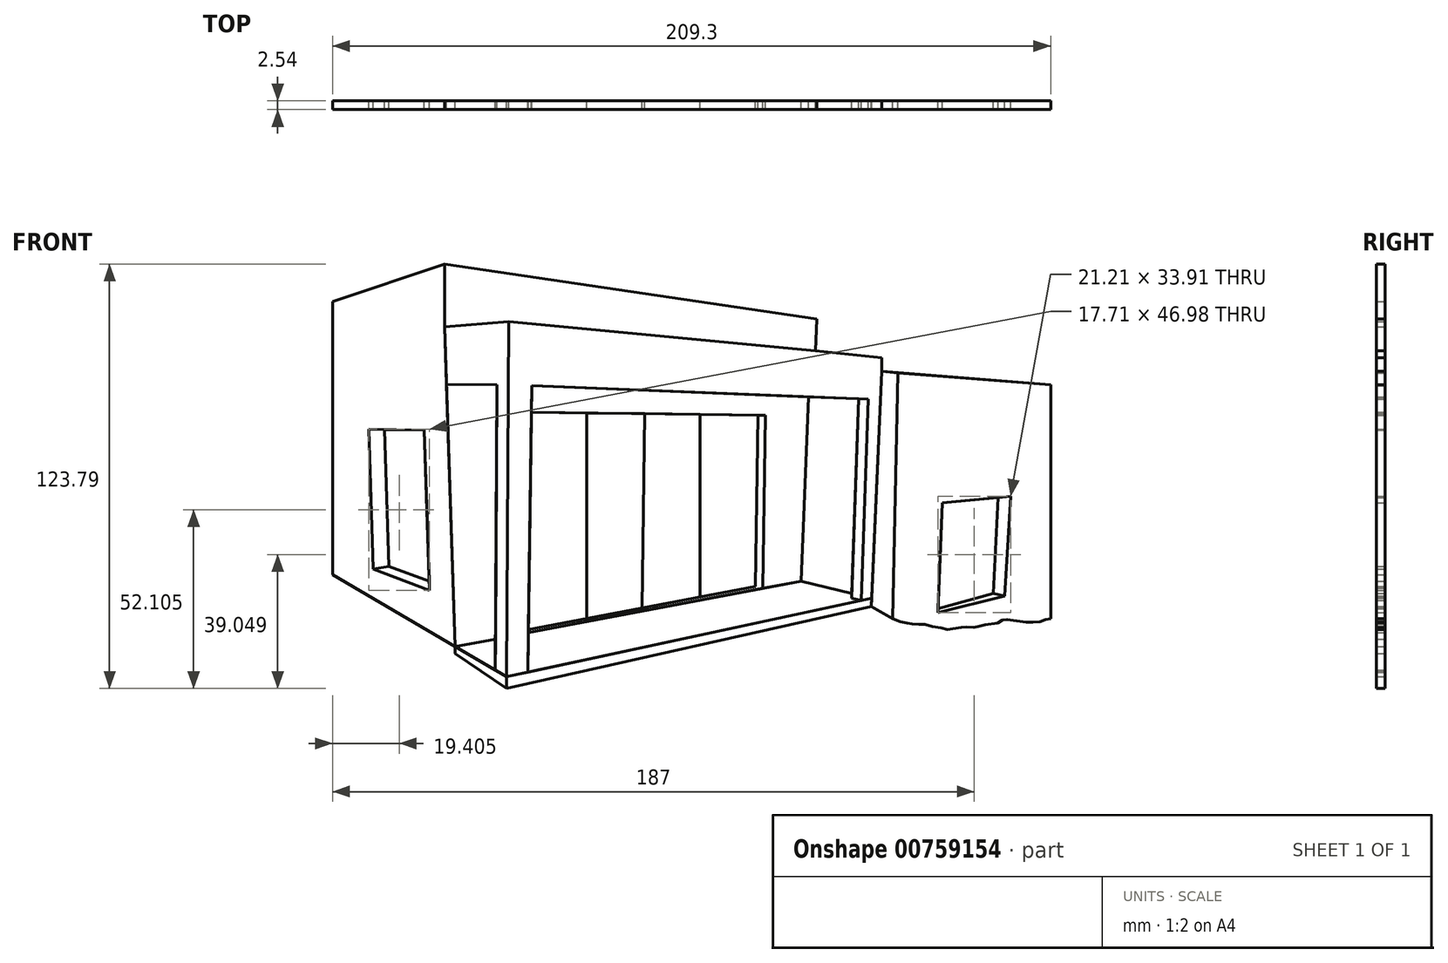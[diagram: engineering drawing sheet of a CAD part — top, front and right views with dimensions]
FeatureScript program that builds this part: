
annotation { "Feature Type Name" : "Feature", "Feature Type Description" : "" }
export const myFeature = defineFeature(function(context is Context, id is Id, definition is map)
    precondition{}
    {
        {
            var Q0;
            Q0=qCreatedBy(makeId("Front.planeOp"),FACE);
            var sketch = newSketch(context, id + "F0", { "sketchPlane" : qUnion([Q0])});
            skSolve(sketch);
        }
        {
            var Q0;
            Q0=qCreatedBy(makeId("Front.planeOp"),FACE);
            var sketch = newSketch(context, id + "F1", { "sketchPlane" : qUnion([Q0])});
            skPoint(sketch, "E0.0", {"position": v(-106.72, 78.02) * mm});
            skPoint(sketch, "E1.0", {"position": v(102.58, 78.02) * mm});
            skPoint(sketch, "E2.0", {"position": v(102.58, -78.96) * mm});
            skPoint(sketch, "E3.0", {"position": v(-106.72, -78.96) * mm});
            skLineSegment(sketch, "E4", {"start": v(-106.72, 78.02) * mm, "end": v(102.58, 78.02) * mm});
            skLineSegment(sketch, "E5", {"start": v(102.58, 78.02) * mm, "end": v(102.58, -78.96) * mm});
            skLineSegment(sketch, "E6", {"start": v(102.58, -78.96) * mm, "end": v(-106.72, -78.96) * mm});
            skLineSegment(sketch, "E7", {"start": v(-106.72, -78.96) * mm, "end": v(-106.72, 78.02) * mm});
            skLineSegment(sketch, "E8", {"start": v(-106.72, 62.84) * mm, "end": v(-74.06, 73.78) * mm});
            skLineSegment(sketch, "E9", {"start": v(-74.06, 73.78) * mm, "end": v(34.35, 57.7) * mm});
            skLineSegment(sketch, "E10", {"start": v(34.35, 57.7) * mm, "end": v(34.04, 48.47) * mm});
            skLineSegment(sketch, "E11", {"start": v(34.04, 48.47) * mm, "end": v(53.34, 46.39) * mm});
            skLineSegment(sketch, "E12", {"start": v(53.34, 46.39) * mm, "end": v(53.34, 42.5) * mm});
            skLineSegment(sketch, "E13", {"start": v(53.34, 42.5) * mm, "end": v(57.96, 41.92) * mm});
            skLineSegment(sketch, "E14", {"start": v(57.96, 41.92) * mm, "end": v(102.58, 38.55) * mm});
            skLineSegment(sketch, "E15", {"start": v(57.96, 41.92) * mm, "end": v(56.56, -29.63) * mm});
            skLineSegment(sketch, "E16", {"start": v(70.93, 4.17) * mm, "end": v(69.68, -27.92) * mm});
            skLineSegment(sketch, "E17", {"start": v(69.68, -27.92) * mm, "end": v(89.2, -23) * mm});
            skLineSegment(sketch, "E18", {"start": v(89.2, -23) * mm, "end": v(90.88, 6) * mm});
            skLineSegment(sketch, "E19", {"start": v(90.88, 6) * mm, "end": v(70.93, 4.17) * mm});
            skLineSegment(sketch, "E20", {"start": v(85.86, -22.34) * mm, "end": v(89.2, -23) * mm});
            skLineSegment(sketch, "E21", {"start": v(-74.06, 73.78) * mm, "end": v(-74.06, 55.43) * mm});
            skLineSegment(sketch, "E22", {"start": v(-74.06, 55.43) * mm, "end": v(-55.39, 57.02) * mm});
            skLineSegment(sketch, "E23", {"start": v(-55.39, 57.02) * mm, "end": v(34.04, 48.47) * mm});
            skLineSegment(sketch, "E24", {"start": v(-49.82, -45) * mm, "end": v(-48.69, 38.29) * mm});
            skLineSegment(sketch, "E25", {"start": v(-48.69, 38.29) * mm, "end": v(49.42, 34.34) * mm});
            skLineSegment(sketch, "E26", {"start": v(53.34, 42.5) * mm, "end": v(50.25, -26.04) * mm});
            skLineSegment(sketch, "E27", {"start": v(50.25, -26.04) * mm, "end": v(56.56, -29.63) * mm});
            skLineSegment(sketch, "E28", {"start": v(53.34, 42.5) * mm, "end": v(102.58, 38.55) * mm});
            skLineSegment(sketch, "E29", {"start": v(47.33, -24.3) * mm, "end": v(49.42, 34.34) * mm});
            skLineSegment(sketch, "E30", {"start": v(-106.72, -16.86) * mm, "end": v(-70.99, -37.79) * mm});
            skLineSegment(sketch, "E31", {"start": v(-70.99, -37.79) * mm, "end": v(-74.06, 55.43) * mm});
            skLineSegment(sketch, "E32", {"start": v(50.25, -26.04) * mm, "end": v(-51.74, -49.05) * mm});
            skLineSegment(sketch, "E33", {"start": v(50.36, -23.64) * mm, "end": v(-56, -46.56) * mm});
            skLineSegment(sketch, "E34", {"start": v(-70.99, -37.79) * mm, "end": v(-56, -46.56) * mm});
            skLineSegment(sketch, "E35", {"start": v(-56, -46.56) * mm, "end": v(-55.5, 38.54) * mm});
            skLineSegment(sketch, "E36", {"start": v(-58.8, 38.56) * mm, "end": v(-73.5, 38.64) * mm});
            skLineSegment(sketch, "E37", {"start": v(-55.5, 38.54) * mm, "end": v(-55.39, 57.02) * mm});
            skLineSegment(sketch, "E38", {"start": v(-80, 25.4) * mm, "end": v(-78.46, -21.4) * mm});
            skLineSegment(sketch, "E39", {"start": v(-78.46, -21.4) * mm, "end": v(-94.83, -15.13) * mm});
            skLineSegment(sketch, "E40", {"start": v(-94.83, -15.13) * mm, "end": v(-96.17, 25.59) * mm});
            skLineSegment(sketch, "E41", {"start": v(-96.17, 25.59) * mm, "end": v(-80, 25.4) * mm});
            skLineSegment(sketch, "E42", {"start": v(-94.83, -15.13) * mm, "end": v(-90.28, -14.41) * mm});
            skLineSegment(sketch, "E43", {"start": v(29.88, -18.67) * mm, "end": v(32.04, 35.04) * mm});
            skLineSegment(sketch, "E44", {"start": v(29.88, -18.67) * mm, "end": v(44.61, -22.24) * mm});
            skLineSegment(sketch, "E45", {"start": v(29.88, -18.67) * mm, "end": v(-49.67, -33.74) * mm});
            skLineSegment(sketch, "E46", {"start": v(-59.3, -44.63) * mm, "end": v(-58.8, 38.56) * mm});
            skLineSegment(sketch, "E47", {"start": v(47.33, -24.3) * mm, "end": v(44.56, -23.62) * mm});
            skLineSegment(sketch, "E48", {"start": v(44.56, -23.62) * mm, "end": v(46.64, 34.45) * mm});
            skLineSegment(sketch, "E49", {"start": v(-56, -46.56) * mm, "end": v(-56, -50.01) * mm});
            skLineSegment(sketch, "E50", {"start": v(-51.74, -49.05) * mm, "end": v(-56, -50.01) * mm});
            skLineSegment(sketch, "E51", {"start": v(-56, -50.01) * mm, "end": v(-70.99, -39.84) * mm});
            skLineSegment(sketch, "E52", {"start": v(-70.99, -39.84) * mm, "end": v(-70.99, -37.79) * mm});
            skLineSegment(sketch, "E53.trimOffspring", {"start": v(-59.24, -35.56) * mm, "end": v(-70.99, -37.79) * mm});
            skLineSegment(sketch, "E54", {"start": v(-48.8, 30.57) * mm, "end": v(19.35, 29.64) * mm});
            skLineSegment(sketch, "E55", {"start": v(19.35, 29.64) * mm, "end": v(18.66, -20.8) * mm});
            skLineSegment(sketch, "E56", {"start": v(18.66, -20.8) * mm, "end": v(16.55, -20.28) * mm});
            skLineSegment(sketch, "E57", {"start": v(16.55, -20.28) * mm, "end": v(17.23, 29.67) * mm});
            skLineSegment(sketch, "E58", {"start": v(16.55, -20.28) * mm, "end": v(-49.66, -32.83) * mm});
            skPoint(sketch, "E59", {"position": v(-16.55, -26.55) * mm});
            skLineSegment(sketch, "E60", {"start": v(-16.55, -26.55) * mm, "end": v(-15.78, 30.1) * mm});
            skPoint(sketch, "E60.endSnap0", {"position": v(-14.72, 30.1) * mm});
            skLineSegment(sketch, "E61", {"start": v(0.32, 29.9) * mm, "end": v(0.32, -23.35) * mm});
            skLineSegment(sketch, "E62", {"start": v(-32.7, 0.1) * mm, "end": v(-32.7, 30.35) * mm});
            skLineSegment(sketch, "E63", {"start": v(-32.7, 30.35) * mm, "end": v(-32.7, -29.61) * mm});
            skFitSpline(sketch, "E64", {"points": [v(56.56, -29.63) * mm, v(58.65, -30.57) * mm, v(60.12, -30.68) * mm, v(61.48, -31.2) * mm, v(62.1, -31.2) * mm, v(63.62, -31.25) * mm, v(64.87, -31.3) * mm, v(66.07, -31.36) * mm, v(68, -31.88) * mm, v(70.57, -32.35) * mm, v(72.12, -32.87) * mm, v(73.49, -32.54) * mm, v(74.26, -32.5) * mm, v(76.7, -32.13) * mm, v(77.4, -32.06) * mm, v(78.47, -32.06) * mm, v(80.36, -32.13) * mm, v(80.91, -32.06) * mm, v(81.46, -31.87) * mm, v(82.46, -31.54) * mm, v(87.38, -30.83) * mm, v(88.19, -30.31) * mm, v(88.92, -29.95) * mm, v(89.31, -29.9) * mm, v(90.88, -29.95) * mm, v(94.9, -30.72) * mm, v(96, -30.62) * mm, v(97.98, -30.62) * mm, v(99.55, -30.57) * mm, v(100.8, -30.2) * mm, v(101.58, -29.63) * mm, v(102.58, -29.63) * mm], "startDerivative": vector(52.93, -29.96) * mm, "endDerivative": vector(39.36, -6.16) * mm});
            skLineSegment(sketch, "E65", {"start": v(-49.82, -45) * mm, "end": v(-49.82, -45.23) * mm});
            skLineSegment(sketch, "E66", {"start": v(-15.78, 30.1) * mm, "end": v(-15.78, 30.12) * mm});
            skLineSegment(sketch, "E67", {"start": v(-78.55, -18.72) * mm, "end": v(-90.28, -14.41) * mm});
            skLineSegment(sketch, "E68", {"start": v(-90.28, -14.41) * mm, "end": v(-91.6, 25.53) * mm});
            skPoint(sketch, "E69.start.orphan", {"position": v(-88.09, 25.5) * mm});
            skLineSegment(sketch, "E70", {"start": v(69.72, -26.75) * mm, "end": v(85.86, -22.34) * mm});
            skLineSegment(sketch, "E71", {"start": v(85.86, -22.34) * mm, "end": v(87.24, 5.45) * mm});
            skLineSegment(sketch, "E72", {"start": v(87.24, 5.45) * mm, "end": v(87.25, 5.66) * mm});
            skPoint(sketch, "E73.start.orphan", {"position": v(84.93, 5.45) * mm});
            skSolve(sketch);
        }
        {
            var Q0;
            {var subQ1=sQuery(id+"F1.wireOp",EDGE,"E8");Q0=makeQuery(id+"F1.imprint","IMPRINT",FACE,{"disambiguationData":[TD([[makeQuery(id+"F1.imprint","IMPRINT",EDGE,{"derivedFrom":subQ1}),-1.0]])]});}
            extrude(context, id + "F2", {"entities" : qUnion([Q0]), "depth" : 2.54 * mm, "offsetDistance" : 25.4 * mm});
        }
        {
            var Q0;
            Q0=makeQuery(id+"F1.imprint","IMPRINT",FACE,{"disambiguationData":[TD([[makeQuery(id+"F1.imprint","IMPRINT",EDGE,{"derivedFrom":sQuery(id+"F1.wireOp",EDGE,"E9")}),-1.0]])]});
            extrude(context, id + "F3", {"entities" : qUnion([Q0]), "depth" : 2.54 * mm, "offsetDistance" : 25.4 * mm});
        }
        {
            var Q0;
            {var subQ4=sQuery(id+"F1.wireOp",EDGE,"E14");Q0=makeQuery(id+"F1.imprint","IMPRINT",FACE,{"disambiguationData":[TD([[makeQuery(id+"F1.imprint","IMPRINT",EDGE,{"derivedFrom":subQ4}),-1.0]])]});}
            extrude(context, id + "F4", {"entities" : qUnion([Q0]), "depth" : 2.54 * mm, "offsetDistance" : 25.4 * mm});
        }
        {
            var Q0;
            {var subQ2=sQuery(id+"F1.wireOp",EDGE,"E36");Q0=makeQuery(id+"F1.imprint","IMPRINT",FACE,{"disambiguationData":[TD([[makeQuery(id+"F1.imprint","IMPRINT",EDGE,{"derivedFrom":subQ2}),1.0]])]});}
            var Q1;
            {var subQ0=sQuery(id+"F1.wireOp",EDGE,"E43");Q1=makeQuery(id+"F1.imprint","IMPRINT",FACE,{"disambiguationData":[TD([[makeQuery(id+"F1.imprint","IMPRINT",EDGE,{"derivedFrom":subQ0}),1.0]])]});}
            extrude(context, id + "F5", {"entities" : qUnion([Q0, Q1]), "depth" : 2.54 * mm, "offsetDistance" : 25.4 * mm});
        }
        {
            var Q0;
            {var subQ5=sQuery(id+"F1.wireOp",EDGE,"E22");Q0=makeQuery(id+"F1.imprint","IMPRINT",FACE,{"disambiguationData":[TD([[makeQuery(id+"F1.imprint","IMPRINT",EDGE,{"derivedFrom":subQ5}),-1.0]])]});}
            extrude(context, id + "F6", {"entities" : qUnion([Q0]), "depth" : 2.54 * mm, "offsetDistance" : 25.4 * mm});
        }
        {
            var Q0;
            Q0=makeQuery(id+"F1.imprint","IMPRINT",FACE,{"disambiguationData":[TD([[makeQuery(id+"F1.imprint","IMPRINT",EDGE,{"derivedFrom":sQuery(id+"F1.wireOp",EDGE,"E11")}),-1.0]])]});
            extrude(context, id + "F7", {"entities" : qUnion([Q0]), "depth" : 2.54 * mm, "offsetDistance" : 25.4 * mm});
        }
        {
            var Q0;
            {var subQ3=sQuery(id+"F1.wireOp",EDGE,"E13");Q0=makeQuery(id+"F1.imprint","IMPRINT",FACE,{"disambiguationData":[TD([[makeQuery(id+"F1.imprint","IMPRINT",EDGE,{"derivedFrom":subQ3}),-1.0]])]});}
            var Q1;
            {var subQ0=sQuery(id+"F1.wireOp",EDGE,"E43");Q1=makeQuery(id+"F1.imprint","IMPRINT",FACE,{"disambiguationData":[TD([[makeQuery(id+"F1.imprint","IMPRINT",EDGE,{"derivedFrom":subQ0}),-1.0]])]});}
            extrude(context, id + "F8", {"entities" : qUnion([Q0, Q1]), "depth" : 2.54 * mm, "offsetDistance" : 25.4 * mm});
        }
        {
            var Q0;
            {var subQ3=sQuery(id+"F1.wireOp",EDGE,"E29");Q0=makeQuery(id+"F1.imprint","IMPRINT",FACE,{"disambiguationData":[TD([[makeQuery(id+"F1.imprint","IMPRINT",EDGE,{"derivedFrom":subQ3}),1.0]])]});}
            extrude(context, id + "F9", {"entities" : qUnion([Q0]), "depth" : 2.54 * mm, "offsetDistance" : 25.4 * mm});
        }
        {
            var Q0;
            {var subQ0=sQuery(id+"F1.wireOp",EDGE,"E53.trimOffspring");Q0=makeQuery(id+"F1.imprint","IMPRINT",FACE,{"disambiguationData":[TD([[makeQuery(id+"F1.imprint","IMPRINT",EDGE,{"derivedFrom":subQ0}),1.0]])]});}
            var Q1;
            {var subQ0=sQuery(id+"F1.wireOp",EDGE,"E44");Q1=makeQuery(id+"F1.imprint","IMPRINT",FACE,{"disambiguationData":[TD([[makeQuery(id+"F1.imprint","IMPRINT",EDGE,{"derivedFrom":subQ0}),-1.0]])]});}
            extrude(context, id + "F10", {"entities" : qUnion([Q0, Q1]), "depth" : 2.54 * mm, "offsetDistance" : 25.4 * mm});
        }
        {
            var Q0;
            {var subQ0=sQuery(id+"F1.wireOp",EDGE,"E49");Q0=makeQuery(id+"F1.imprint","IMPRINT",FACE,{"disambiguationData":[TD([[makeQuery(id+"F1.imprint","IMPRINT",EDGE,{"derivedFrom":subQ0}),-1.0]])]});}
            extrude(context, id + "F11", {"entities" : qUnion([Q0]), "depth" : 2.54 * mm, "offsetDistance" : 25.4 * mm});
        }
        {
            var Q0;
            {var subQ5=sQuery(id+"F1.wireOp",EDGE,"E32");Q0=makeQuery(id+"F1.imprint","IMPRINT",FACE,{"disambiguationData":[TD([[makeQuery(id+"F1.imprint","IMPRINT",EDGE,{"derivedFrom":subQ5}),-1.0]])]});}
            extrude(context, id + "F12", {"entities" : qUnion([Q0]), "depth" : 2.54 * mm, "offsetDistance" : 25.4 * mm});
        }
        {
            var Q0;
            {var subQ0=sQuery(id+"F1.wireOp",EDGE,"E55");Q0=makeQuery(id+"F1.imprint","IMPRINT",FACE,{"disambiguationData":[TD([[makeQuery(id+"F1.imprint","IMPRINT",EDGE,{"derivedFrom":subQ0}),-1.0]])]});}
            var Q1;
            {var subQ1=sQuery(id+"F1.wireOp",EDGE,"E56");Q1=makeQuery(id+"F1.imprint","IMPRINT",FACE,{"disambiguationData":[TD([[makeQuery(id+"F1.imprint","IMPRINT",EDGE,{"derivedFrom":subQ1}),1.0]])]});}
            extrude(context, id + "F13", {"entities" : qUnion([Q0, Q1]), "depth" : 2.54 * mm, "offsetDistance" : 25.4 * mm});
        }
        {
            var Q0;
            {var subQ0=sQuery(id+"F1.wireOp",EDGE,"E63");var subQ3=makeQuery(id+"F1.imprint","IMPRINT",VERTEX,{"derivedFrom":subQ0});Q0=makeQuery(id+"F1.imprint","IMPRINT",FACE,{"disambiguationData":[TD([[makeQuery(id+"F1.imprint","IMPRINT",EDGE,{"disambiguationData":[TD([[subQ3,1.0]])],"derivedFrom":subQ0}),-1.0]])]});}
            extrude(context, id + "F14", {"entities" : qUnion([Q0]), "depth" : 2.54 * mm, "offsetDistance" : 25.4 * mm});
        }
        {
            var Q0;
            {var subQ4=sQuery(id+"F1.wireOp",EDGE,"E60");Q0=makeQuery(id+"F1.imprint","IMPRINT",FACE,{"disambiguationData":[TD([[makeQuery(id+"F1.imprint","IMPRINT",EDGE,{"derivedFrom":subQ4}),1.0]])]});}
            extrude(context, id + "F15", {"entities" : qUnion([Q0]), "depth" : 2.54 * mm, "offsetDistance" : 25.4 * mm});
        }
        {
            var Q0;
            {var subQ3=sQuery(id+"F1.wireOp",EDGE,"E60");Q0=makeQuery(id+"F1.imprint","IMPRINT",FACE,{"disambiguationData":[TD([[makeQuery(id+"F1.imprint","IMPRINT",EDGE,{"derivedFrom":subQ3}),-1.0]])]});}
            extrude(context, id + "F16", {"entities" : qUnion([Q0]), "depth" : 2.54 * mm, "offsetDistance" : 25.4 * mm});
        }
        {
            var Q0;
            {var subQ0=sQuery(id+"F1.wireOp",EDGE,"E57");Q0=makeQuery(id+"F1.imprint","IMPRINT",FACE,{"disambiguationData":[TD([[makeQuery(id+"F1.imprint","IMPRINT",EDGE,{"derivedFrom":subQ0}),1.0]])]});}
            extrude(context, id + "F17", {"entities" : qUnion([Q0]), "depth" : 2.54 * mm, "offsetDistance" : 25.4 * mm});
        }
        {
            var Q0;
            {var subQ0=sQuery(id+"F1.wireOp",EDGE,"E40");Q0=makeQuery(id+"F1.imprint","IMPRINT",FACE,{"disambiguationData":[TD([[makeQuery(id+"F1.imprint","IMPRINT",EDGE,{"derivedFrom":subQ0}),-1.0]])]});}
            extrude(context, id + "F18", {"entities" : qUnion([Q0]), "depth" : 2.54 * mm, "offsetDistance" : 25.4 * mm});
        }
        {
            var Q0;
            {var subQ0=sQuery(id+"F1.wireOp",EDGE,"E39");Q0=makeQuery(id+"F1.imprint","IMPRINT",FACE,{"disambiguationData":[TD([[makeQuery(id+"F1.imprint","IMPRINT",EDGE,{"derivedFrom":subQ0}),-1.0]])]});}
            extrude(context, id + "F19", {"entities" : qUnion([Q0]), "depth" : 2.54 * mm, "offsetDistance" : 25.4 * mm});
        }
        {
            var Q0;
            {var subQ1=sQuery(id+"F1.wireOp",EDGE,"E18");Q0=makeQuery(id+"F1.imprint","IMPRINT",FACE,{"disambiguationData":[TD([[makeQuery(id+"F1.imprint","IMPRINT",EDGE,{"derivedFrom":subQ1}),1.0]])]});}
            extrude(context, id + "F20", {"entities" : qUnion([Q0]), "depth" : 2.54 * mm, "offsetDistance" : 25.4 * mm});
        }
        {
            var Q0;
            {var subQ0=sQuery(id+"F1.wireOp",EDGE,"E17");Q0=makeQuery(id+"F1.imprint","IMPRINT",FACE,{"disambiguationData":[TD([[makeQuery(id+"F1.imprint","IMPRINT",EDGE,{"derivedFrom":subQ0}),1.0]])]});}
            extrude(context, id + "F21", {"entities" : qUnion([Q0]), "depth" : 2.54 * mm, "offsetDistance" : 25.4 * mm});
        }
        {
            var Q0;
            {var subQ3=sQuery(id+"F1.wireOp",EDGE,"E67");Q0=makeQuery(id+"F1.imprint","IMPRINT",FACE,{"disambiguationData":[TD([[makeQuery(id+"F1.imprint","IMPRINT",EDGE,{"derivedFrom":subQ3}),-1.0]])]});}
            var Q1;
            {var subQ3=sQuery(id+"F1.wireOp",EDGE,"E70");Q1=makeQuery(id+"F1.imprint","IMPRINT",FACE,{"disambiguationData":[TD([[makeQuery(id+"F1.imprint","IMPRINT",EDGE,{"derivedFrom":subQ3}),1.0]])]});}
            extrude(context, id + "F22", {"entities" : qUnion([Q0, Q1]), "depth" : 2.54 * mm, "offsetDistance" : 25.4 * mm});
        }
        {
            var Q0;
            Q0=makeQuery(id+"F1.imprint","IMPRINT",FACE,{"disambiguationData":[TD([[makeQuery(id+"F1.imprint","IMPRINT",EDGE,{"derivedFrom":sQuery(id+"F1.wireOp",EDGE,"E13")}),1.0]])]});
            extrude(context, id + "F23", {"entities" : qUnion([Q0]), "depth" : 2.54 * mm, "offsetDistance" : 25.4 * mm});
        }
    });
